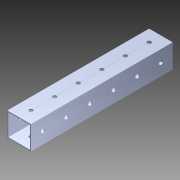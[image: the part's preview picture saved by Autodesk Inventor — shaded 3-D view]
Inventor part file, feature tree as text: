
AUTODESK INVENTOR PART (.ipt)
format: ipt  version: 2014 (Build 180170000, 170)  size: 1,140,736 bytes
history: native  units: in
note: dims shown in document units (in); Inventor stores cm internally (conversion verified against a paired STEP export)
features: pattern_circular x1, other x1, plane x1, extrude x1, imported_body x1, sketch x1
ambient origin geometry x8: Origin, YZ Plane, XZ Plane, XY Plane, X Axis, Y Axis, Z Axis, Center Point
bodies: Body1 (feature_tree)
feature tree (6):
  pattern_circular  "CirPattern2"
  other  "217-3426-STEP1"
  plane  "Work Plane1"
  extrude  "Extrusion1"  Depth=3937.0079in TaperAngle=0.0deg
  imported_body  "Base1"
  sketch  "Sketch1"  dims[d0=-6.0in d1=3937.0079in d2=0.0in]
